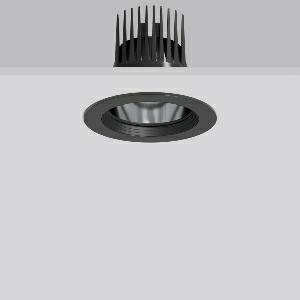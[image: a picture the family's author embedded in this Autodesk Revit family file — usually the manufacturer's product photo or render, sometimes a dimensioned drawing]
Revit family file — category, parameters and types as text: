
# Revit family: heledon_maxi_e_901765_003_1_76_9c36
name_source: partatom
category: Lighting Fixtures
units: mm (PartAtom-declared; Revit-internal decimal feet)

## family parameters
Cut with Voids When Loaded = No
Host = Face
Light Source = No
Part Type = Normal
Room Calculation Point = No
Round Connector Dimension = Use Diameter
Shared = No

## types (1)
- HELEDON maxi E (1 x LED Modul 940, 4550 lm, 4000)
    Apparent Load = 35 VA
    Approval mark = CE
    CIE Flux Codes = 100 100 100 100 100
    Color Rendering = 92
    Color Temperature = 4000
    Default Elevation = 1800 mm
    Description = Series: HELEDON maxi
Round recessed downlight. Housing: die-cast aluminium, powder-coated. Black plastic ring and recessed LED to prevent glare from the side. Optical assembly with reflector made of MIRO-Silver with 98% total light reflection for outstanding efficiency - can be changed without tools. Best colour rendering index Ra>90. Suitable for Recessed ceiling mounting. Installation without tools thanks to spring fastening system. Including separate LED converter with connecting cable 600 mm.High quality converter without flickering and stroboscopic effect. Through-wiring box (5 pole) available as accessory. The following accessories can be mounted without use of tools: interchangeable lenses, decorative glasses, honeycomb louvre, clear and frosted diffusers, white interchangeable plastic ring. 
Colour: deep black, matt (RAL 9005)
Diameter: 162 mm
Height: 3 mm
Cut-out diameter: 152 mm
Recess height: 200 mm
Luminaire: recess height: 135 mm
Lamp: LED
Socket: without socket
Colour temperature: 4000K
Colour rendering index (CRI): 92
System power: 35 W
Rated luminous flux: 4550 lm
Luminous efficiency: 130 lm/W
Control gear: Converter, dimmable, DALI
Protection class: II
Type of protection: IP 20
    Height = 0 mm  [stored 0 ft]
    Lamp = 1 x LED Modul 940
    Lamp Light Flux = 4550 lm
    Lamp count = 1
    Length = 162 mm
    Lifetime = 50000 h
    Luminous efficacy = 130 lm/W
    Manufacturer = RZB
    ModVariant = No
    Model = 901765.003.1.76
    Mounting Place = Ceiling
    Mounting Type = Recessed
    Number of Poles = 1
    OnlyDefault = Yes
    Power Factor = 1
    Product Name = HELEDON maxi E
    Product group = Recessed downlights
    ProductGroupID = 402
    Protection Class = Protection class II
    Protection Degree = IP 20
    RLX_Detail_Level = 1
    RLX_Emergency_Light_Flux = 0 lm
    RLX_Emergency_Type = 0
    RLX_Emergency_Type_DB = No
    RlxData = <blob elided: 121617 chars, md5=7cd62edb>
    Socket = socket
    Standby Power = 0 W
    System Light Flux = 4550 lm
    System Power = 35 W
    Type Comments = Product without accessories
    Type Image = 901662.003.jpg
    URL = http://relux.com
    VarID = ---
    Voltage = 230 V
    Voltage Range = 220-240 V
    Weight = 0.00 kg
    Width = 0 mm  [stored 0 ft]

note: [stored X ft] marks values corroborated as IEEE doubles in the binary element streams (Revit-internal decimal feet)

## geometry (parser evidence)
native form markers: Blend x4, Sweep x13
no freeform markers — native parametric forms only
